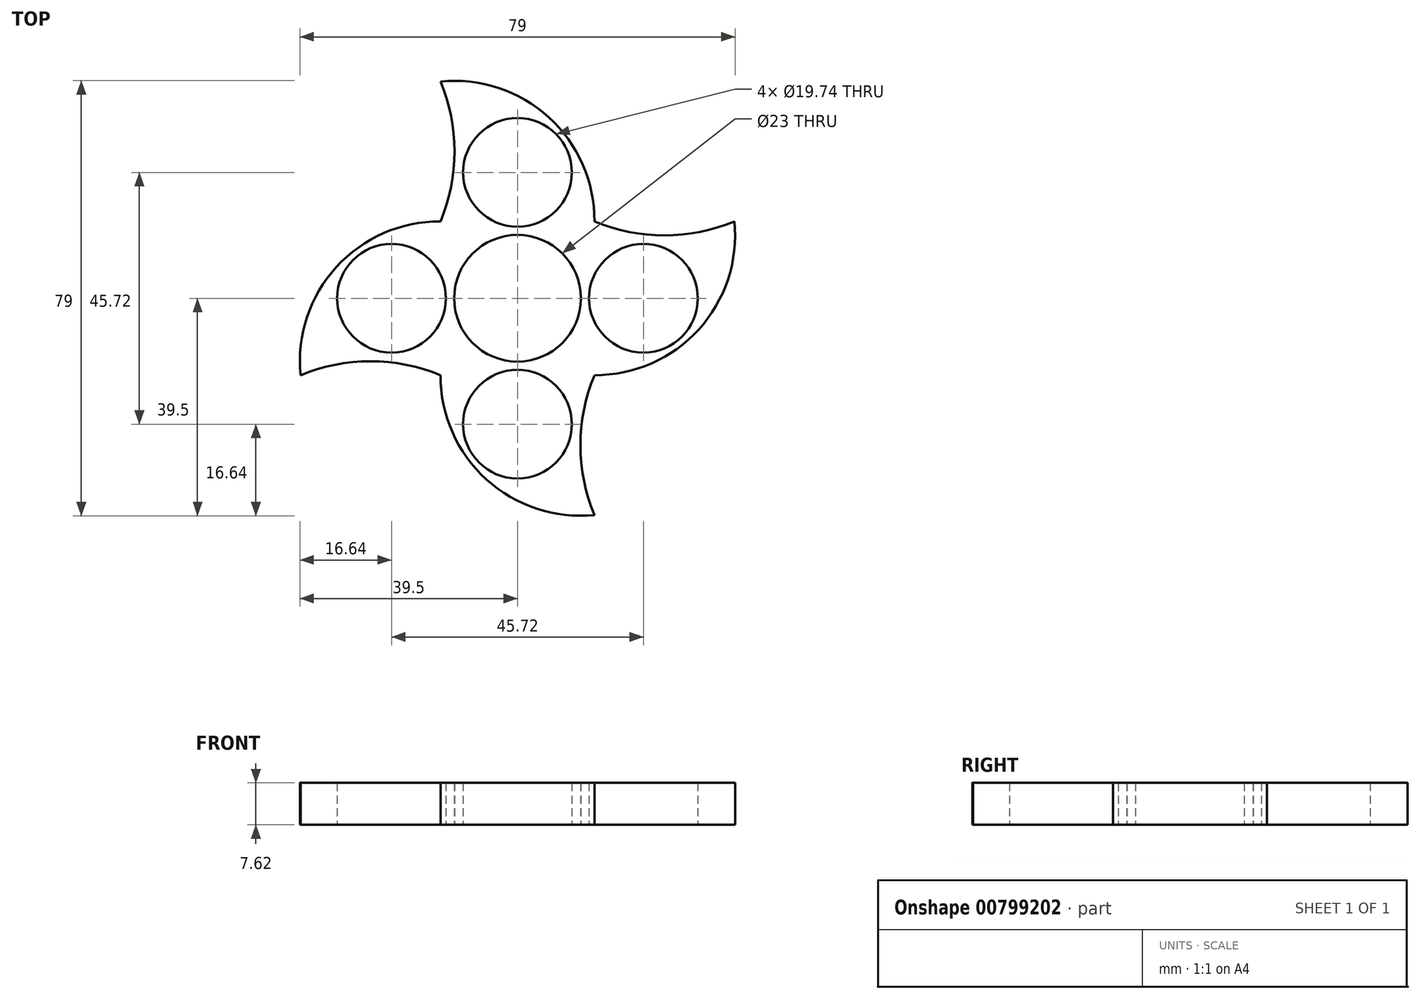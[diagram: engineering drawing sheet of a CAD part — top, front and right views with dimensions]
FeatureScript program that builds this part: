
annotation { "Feature Type Name" : "Feature", "Feature Type Description" : "" }
export const myFeature = defineFeature(function(context is Context, id is Id, definition is map)
    precondition{}
    {
        {
            var Q0;
            Q0=qCreatedBy(makeId("Top.planeOp"),FACE);
            var sketch = newSketch(context, id + "F0", { "sketchPlane" : qUnion([Q0])});
            skCircle(sketch, "E0", {"center": v(0, 0) * mm, "radius": 11.5 * mm});
            skLineSegment(sketch, "E1.bottom", {"start": v(13.97, -13.97) * mm, "end": v(-13.97, -13.97) * mm});
            skLineSegment(sketch, "E1.top", {"start": v(13.97, 13.97) * mm, "end": v(-13.97, 13.97) * mm});
            skLineSegment(sketch, "E1.left", {"start": v(13.97, -13.97) * mm, "end": v(13.97, 13.97) * mm});
            skLineSegment(sketch, "E1.right", {"start": v(-13.97, -13.97) * mm, "end": v(-13.97, 13.97) * mm});
            skArc(sketch, "E2", {"start": v(-13.97, 13.97) * mm, "mid": v(-11.43, 26.67) * mm, "end": v(-13.97, 39.37) * mm});
            skArc(sketch, "E3", {"start": v(13.97, 13.97) * mm, "mid": v(5.66, 32.9) * mm, "end": v(-13.97, 39.37) * mm});
            skArc(sketch, "E4", {"start": v(13.97, 13.97) * mm, "mid": v(26.67, 11.43) * mm, "end": v(39.37, 13.97) * mm});
            skArc(sketch, "E5", {"start": v(13.97, -13.97) * mm, "mid": v(32.9, -5.66) * mm, "end": v(39.37, 13.97) * mm});
            skArc(sketch, "E6", {"start": v(13.97, -13.97) * mm, "mid": v(11.43, -26.67) * mm, "end": v(13.97, -39.37) * mm});
            skArc(sketch, "E7", {"start": v(-13.97, -13.97) * mm, "mid": v(-5.66, -32.9) * mm, "end": v(13.97, -39.37) * mm});
            skArc(sketch, "E8", {"start": v(-13.97, -13.97) * mm, "mid": v(-26.67, -11.43) * mm, "end": v(-39.37, -13.97) * mm});
            skArc(sketch, "E9", {"start": v(-13.97, 13.97) * mm, "mid": v(-32.9, 5.66) * mm, "end": v(-39.37, -13.97) * mm});
            skCircle(sketch, "E10", {"center": v(0, 22.86) * mm, "radius": 9.87 * mm});
            skCircle(sketch, "E11.MirrorC", {"center": v(0, -22.86) * mm, "radius": 9.87 * mm});
            skCircle(sketch, "E12", {"center": v(22.86, 0) * mm, "radius": 9.87 * mm});
            skCircle(sketch, "E13.MirrorC", {"center": v(-22.86, 0) * mm, "radius": 9.87 * mm});
            skSolve(sketch);
        }
        {
            var Q0;
            Q0=makeQuery(id+"F0.imprint","IMPRINT",FACE,{"disambiguationData":[TD([[makeQuery(id+"F0.imprint","IMPRINT",EDGE,{"derivedFrom":sQuery(id+"F0.wireOp",EDGE,"E1.left")}),-1.0]])]});
            var Q1;
            Q1=makeQuery(id+"F0.imprint","IMPRINT",FACE,{"disambiguationData":[TD([[makeQuery(id+"F0.imprint","IMPRINT",EDGE,{"derivedFrom":sQuery(id+"F0.wireOp",EDGE,"E1.top")}),-1.0]])]});
            var Q2;
            Q2=makeQuery(id+"F0.imprint","IMPRINT",FACE,{"disambiguationData":[TD([[makeQuery(id+"F0.imprint","IMPRINT",EDGE,{"derivedFrom":sQuery(id+"F0.wireOp",EDGE,"E1.right")}),1.0]])]});
            var Q3;
            Q3=makeQuery(id+"F0.imprint","IMPRINT",FACE,{"disambiguationData":[TD([[makeQuery(id+"F0.imprint","IMPRINT",EDGE,{"derivedFrom":sQuery(id+"F0.wireOp",EDGE,"E0")}),-1.0]])]});
            var Q4;
            Q4=makeQuery(id+"F0.imprint","IMPRINT",FACE,{"disambiguationData":[TD([[makeQuery(id+"F0.imprint","IMPRINT",EDGE,{"derivedFrom":sQuery(id+"F0.wireOp",EDGE,"E1.bottom")}),1.0]])]});
            extrude(context, id + "F1", {"entities" : qUnion([Q0, Q1, Q2, Q3, Q4]), "depth" : 7.62 * mm, "offsetDistance" : 25.4 * mm});
        }
    });
